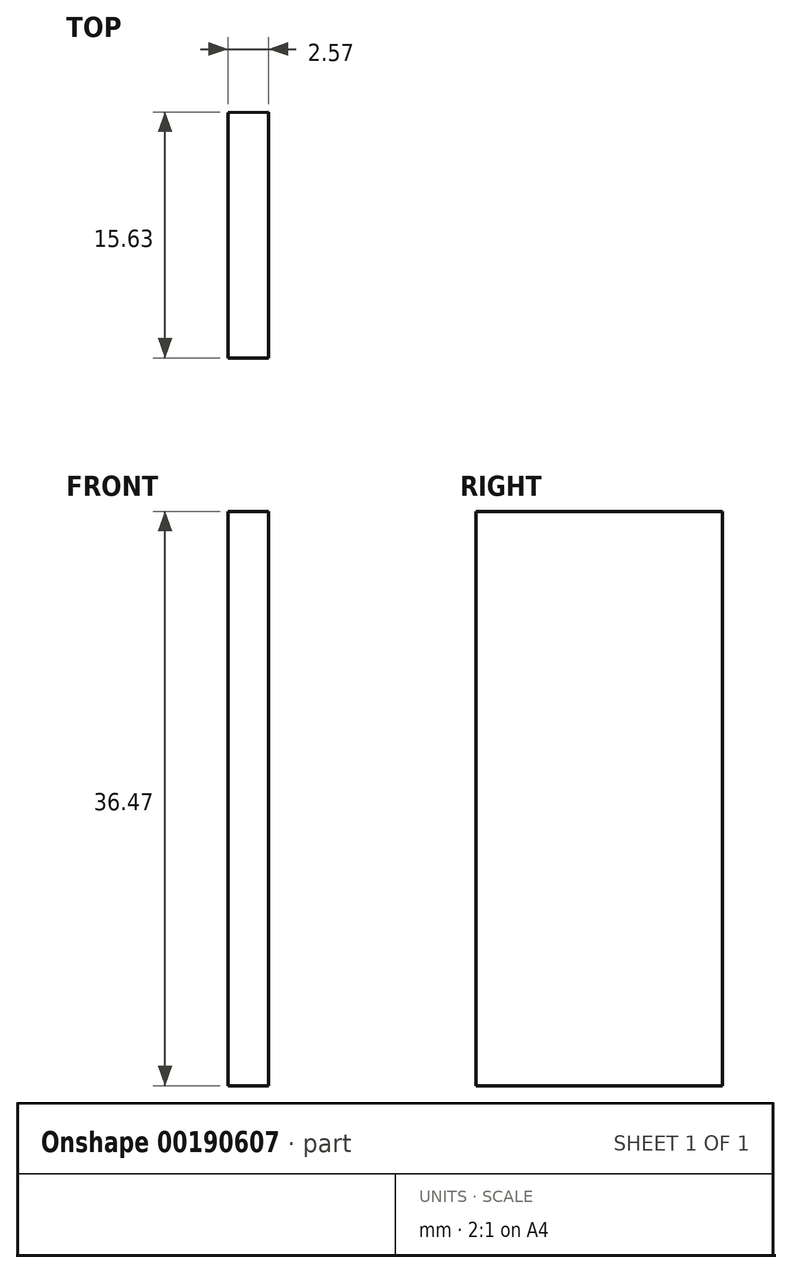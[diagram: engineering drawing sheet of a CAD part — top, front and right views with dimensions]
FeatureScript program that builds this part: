
annotation { "Feature Type Name" : "Feature", "Feature Type Description" : "" }
export const myFeature = defineFeature(function(context is Context, id is Id, definition is map)
    precondition{}
    {
        {
            var Q0;
            Q0=qCreatedBy(makeId("Top.planeOp"),FACE);
            var sketch = newSketch(context, id + "F0", { "sketchPlane" : qUnion([Q0])});
            skLineSegment(sketch, "E0", {"start": v(-18.84, -0.04) * mm, "end": v(-18.84, 8.04) * mm});
            skLineSegment(sketch, "E1", {"start": v(-18.84, 8.04) * mm, "end": v(-6.14, 8.04) * mm});
            skLineSegment(sketch, "E2", {"start": v(-6.14, 8.04) * mm, "end": v(-6.14, -23.71) * mm});
            skLineSegment(sketch, "E3", {"start": v(-6.14, -23.71) * mm, "end": v(-18.84, -23.71) * mm});
            skLineSegment(sketch, "E4", {"start": v(-18.84, -23.71) * mm, "end": v(-18.84, -15.63) * mm});
            skLineSegment(sketch, "E5", {"start": v(-18.84, -15.63) * mm, "end": v(-11.6, -15.63) * mm});
            skLineSegment(sketch, "E6", {"start": v(-11.6, -15.63) * mm, "end": v(-11.6, -0.04) * mm});
            skLineSegment(sketch, "E7", {"start": v(-11.6, -0.04) * mm, "end": v(-18.84, -0.04) * mm});
            skLineSegment(sketch, "E8", {"start": v(-11.6, -15.63) * mm, "end": v(-9.02, -15.63) * mm});
            skLineSegment(sketch, "E9", {"start": v(-9.02, -15.63) * mm, "end": v(-9.02, 0) * mm});
            skLineSegment(sketch, "E10", {"start": v(-9.02, 0) * mm, "end": v(-11.6, -0.04) * mm});
            skSolve(sketch);
        }
        {
            var Q0;
            Q0=makeQuery(id+"F0.imprint","IMPRINT",FACE,{"disambiguationData":[TD([[makeQuery(id+"F0.imprint","IMPRINT",EDGE,{"derivedFrom":sQuery(id+"F0.wireOp",EDGE,"E6")}),-1.0]])]});
            extrude(context, id + "F1", {"entities" : qUnion([Q0]), "depth" : 36.47 * mm});
        }
    });
